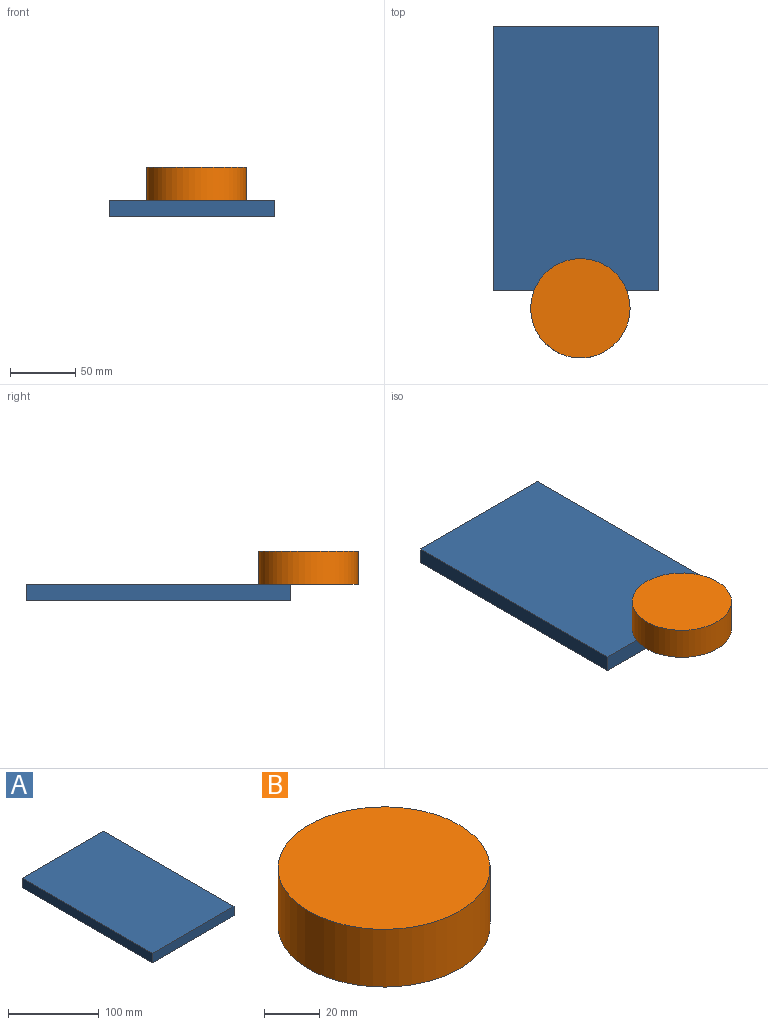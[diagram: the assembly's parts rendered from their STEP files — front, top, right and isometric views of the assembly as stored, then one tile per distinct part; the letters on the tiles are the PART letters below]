
ASSEMBLY  parts=2 mates=1
PART A: 6 faces, bbox 127x203.2x12.7 mm
  f0: plane 203.2x12.7mm, normal (-1,0,0), area 2580.6mm2, adj f1,f3,f4,f5
  f1: plane 127x12.7mm, normal (0,-1,0), area 1612.9mm2, adj f0,f2,f4,f5
  f2: plane 203.2x12.7mm, normal (1,0,0), area 2580.6mm2, adj f1,f3,f4,f5
  f3: plane 127x12.7mm, normal (0,1,0), area 1612.9mm2, adj f0,f2,f4,f5
  f4: plane 203.2x127mm, normal (0,0,1), area 25806.4mm2, adj f0,f1,f2,f3
  f5: plane 203.2x127mm, normal (0,0,-1), area 25806.4mm2, adj f0,f1,f2,f3
PART B: 3 faces, bbox 76.2x76.2x25.4 mm
  f0: cylinder r=38.1mm len=76.2mm, axis (0,0,-1), area 6080.5mm2, adj f1,f2
  f1: plane 76.2x76.2mm, normal (0,0,1), area 4560.4mm2, adj f0
  f2: plane 76.2x76.2mm, normal (0,0,-1), area 4560.4mm2, adj f0
PLACE A rot(axis=(1,0,0),180deg) t=(-63.5,101.6,12.7)mm
PLACE B t=(3.39,-115.07,12.7)mm
MATE planar B.f0 <-> A.f5  axis (0,0,-1) through (3.39,-115.07,12.7)mm
